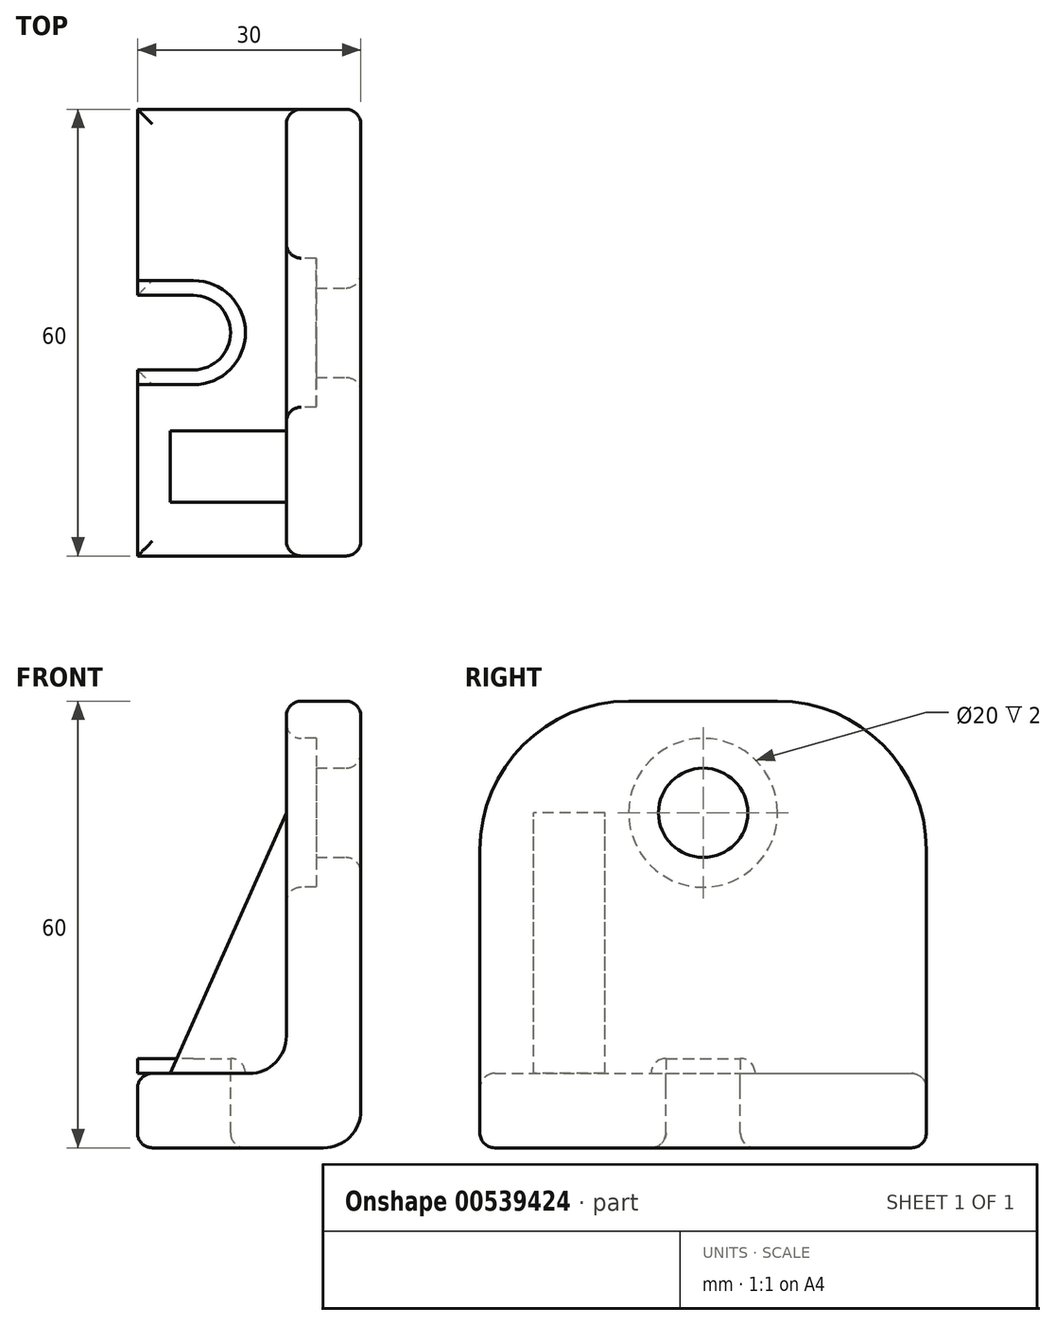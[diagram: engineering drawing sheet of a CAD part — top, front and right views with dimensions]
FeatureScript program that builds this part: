
annotation { "Feature Type Name" : "Feature", "Feature Type Description" : "" }
export const myFeature = defineFeature(function(context is Context, id is Id, definition is map)
    precondition{}
    {
        {
            var Q0;
            Q0=qCreatedBy(makeId("Front.planeOp"),FACE);
            var sketch = newSketch(context, id + "F0", { "sketchPlane" : qUnion([Q0])});
            skLineSegment(sketch, "E0", {"start": v(0, 0) * mm, "end": v(0, 10) * mm});
            skLineSegment(sketch, "E1", {"start": v(0, 10) * mm, "end": v(15, 10) * mm});
            skLineSegment(sketch, "E2", {"start": v(20, 15) * mm, "end": v(20, 60) * mm});
            skLineSegment(sketch, "E3", {"start": v(20, 60) * mm, "end": v(30, 60) * mm});
            skLineSegment(sketch, "E4", {"start": v(30, 60) * mm, "end": v(30, 5) * mm});
            skLineSegment(sketch, "E5", {"start": v(25, 0) * mm, "end": v(0, 0) * mm});
            skPoint(sketch, "E6.visualSharp", {"position": v(20, 10) * mm});
            skArc(sketch, "E6.filletArc", {"start": v(15, 10) * mm, "mid": v(18.54, 11.46) * mm, "end": v(20, 15) * mm});
            skPoint(sketch, "E7.visualSharp", {"position": v(30, 0) * mm});
            skArc(sketch, "E7.filletArc", {"start": v(25, 0) * mm, "mid": v(28.54, 1.46) * mm, "end": v(30, 5) * mm});
            skSolve(sketch);
        }
        {
            var Q0;
            Q0=makeQuery(id+"F0.imprint","IMPRINT",FACE,{"disambiguationData":[TD([[makeQuery(id+"F0.imprint","IMPRINT",EDGE,{"derivedFrom":sQuery(id+"F0.wireOp",EDGE,"E0")}),-1.0]])]});
            extrude(context, id + "F1", {"entities" : qUnion([Q0]), "endBound" : BoundingType.SYMMETRIC, "depth" : 60 * mm, "offsetDistance" : 25 * mm});
        }
        {
            var Q0;
            Q0=makeQuery(id+"F1.opExtrude","SWEPT_FACE",FACE,{"disambiguationData":[OSD([sQuery(id+"F0.wireOp",EDGE,"E4")])]});
            var sketch = newSketch(context, id + "F2", { "sketchPlane" : qUnion([Q0])});
            skCircle(sketch, "E8", {"center": v(0, 45) * mm, "radius": 6 * mm});
            skSolve(sketch);
        }
        {
            var Q0;
            Q0=makeQuery(id+"F2.imprint","IMPRINT",FACE,{"disambiguationData":[TD([[makeQuery(id+"F2.imprint","IMPRINT",EDGE,{"derivedFrom":sQuery(id+"F2.wireOp",EDGE,"E8")}),1.0]])]});
            var Q1;
            Q1=makeQuery(id+"F1.opExtrude","SWEPT_FACE",FACE,{"disambiguationData":[OSD([sQuery(id+"F0.wireOp",EDGE,"E2")])]});
            extrude(context, id + "F3", {"entities" : qUnion([Q0]), "operationType" : NewBodyOperationType.REMOVE, "endBound" : BoundingType.UP_TO_SURFACE, "oppositeDirection" : true, "depth" : 25 * mm, "endBoundEntityFace" : qUnion([Q1]), "offsetDistance" : 25 * mm});
        }
        {
            var Q0;
            Q0=makeQuery(id+"F1.opExtrude","SWEPT_FACE",FACE,{"disambiguationData":[OSD([sQuery(id+"F0.wireOp",EDGE,"E2")])]});
            var sketch = newSketch(context, id + "F4", { "sketchPlane" : qUnion([Q0])});
            skCircle(sketch, "E9", {"center": v(0, 45) * mm, "radius": 10 * mm});
            skSolve(sketch);
        }
        {
            var Q0;
            Q0 = qSketchRegion(id + "F4", true);
            extrude(context, id + "F5", {"entities" : qUnion([Q0]), "operationType" : NewBodyOperationType.REMOVE, "oppositeDirection" : true, "depth" : 4 * mm, "offsetDistance" : 25 * mm});
        }
        {
            var Q0;
            Q0=makeQuery(id+"F1.opExtrude","SWEPT_FACE",FACE,{"disambiguationData":[OSD([sQuery(id+"F0.wireOp",EDGE,"E1")])]});
            var sketch = newSketch(context, id + "F6", { "sketchPlane" : qUnion([Q0])});
            skArc(sketch, "E10", {"start": v(7.5, -5) * mm, "mid": v(12.5, 0) * mm, "end": v(7.5, 5) * mm});
            skLineSegment(sketch, "E11", {"start": v(7.5, 5) * mm, "end": v(0, 5) * mm});
            skLineSegment(sketch, "E12", {"start": v(7.5, -5) * mm, "end": v(0, -5) * mm});
            skLineSegment(sketch, "E13", {"start": v(0, -5) * mm, "end": v(0, 5) * mm});
            skSolve(sketch);
        }
        {
            var Q0;
            Q0=makeQuery(id+"F6.imprint","IMPRINT",FACE,{"disambiguationData":[TD([[makeQuery(id+"F6.imprint","IMPRINT",EDGE,{"derivedFrom":sQuery(id+"F6.wireOp",EDGE,"E10")}),1.0]])]});
            var Q1;
            Q1=makeQuery(id+"F1.opExtrude","SWEPT_FACE",FACE,{"disambiguationData":[OSD([sQuery(id+"F0.wireOp",EDGE,"E5")])]});
            extrude(context, id + "F7", {"entities" : qUnion([Q0]), "operationType" : NewBodyOperationType.REMOVE, "endBound" : BoundingType.UP_TO_SURFACE, "oppositeDirection" : true, "depth" : 25 * mm, "endBoundEntityFace" : qUnion([Q1]), "offsetDistance" : 25 * mm});
        }
        {
            var Q0;
            Q0=qCreatedBy(makeId("Front.planeOp"),FACE);
            cPlane(context, id + "F8", {"entities" : qUnion([Q0]), "cplaneType" : CPlaneType.OFFSET, "offset" : 18 * mm, "width" : 150 * mm, "height" : 150 * mm});
        }
        {
            var Q0;
            Q0=qCreatedBy(id+"F8.planeOp",FACE);
            var sketch = newSketch(context, id + "F9", { "sketchPlane" : qUnion([Q0])});
            skLineSegment(sketch, "E14.0", {"start": v(20, 15) * mm, "end": v(20, 45) * mm});
            skArc(sketch, "E14.1", {"start": v(15, 10) * mm, "mid": v(18.54, 11.46) * mm, "end": v(20, 15) * mm});
            skLineSegment(sketch, "E14.2", {"start": v(4.4, 10) * mm, "end": v(15, 10) * mm});
            skLineSegment(sketch, "E15", {"start": v(4.4, 10) * mm, "end": v(20, 45) * mm});
            skSolve(sketch);
        }
        {
            var Q0;
            Q0 = qSketchRegion(id + "F9", true);
            extrude(context, id + "F10", {"entities" : qUnion([Q0]), "endBound" : BoundingType.SYMMETRIC, "oppositeDirection" : true, "depth" : 9.6 * mm, "offsetDistance" : 25 * mm});
        }
        {
            var Q0;
            Q0=makeQuery(id+"F6.imprint","IMPRINT",FACE,{"disambiguationData":[TD([[makeQuery(id+"F6.imprint","IMPRINT",EDGE,{"derivedFrom":sQuery(id+"F6.wireOp",EDGE,"E10")}),-1.0]])]});
            var sketch = newSketch(context, id + "F11", { "sketchPlane" : qUnion([Q0])});
            skArc(sketch, "E16.0", {"start": v(7.5, -5) * mm, "mid": v(12.5, 0) * mm, "end": v(7.5, 5) * mm});
            skLineSegment(sketch, "E16.1", {"start": v(7.5, -5) * mm, "end": v(0, -5) * mm});
            skLineSegment(sketch, "E16.2", {"start": v(7.5, 5) * mm, "end": v(0, 5) * mm});
            skLineSegment(sketch, "E17.0", {"start": v(7.5, 7) * mm, "end": v(0, 7) * mm});
            skArc(sketch, "E17.1", {"start": v(7.5, -7) * mm, "mid": v(14.5, 0) * mm, "end": v(7.5, 7) * mm});
            skLineSegment(sketch, "E17.2", {"start": v(7.5, -7) * mm, "end": v(0, -7) * mm});
            skLineSegment(sketch, "E18", {"start": v(0, 7) * mm, "end": v(0, 5) * mm});
            skLineSegment(sketch, "E19", {"start": v(0, -5) * mm, "end": v(0, -7) * mm});
            skPoint(sketch, "E16.3.end.orphan", {"position": v(0, 5) * mm});
            skPoint(sketch, "E16.3.start.orphan", {"position": v(0, -5) * mm});
            skSolve(sketch);
        }
        {
            var Q0;
            Q0=makeQuery(id+"F11.imprint","IMPRINT",FACE,{"disambiguationData":[TD([[makeQuery(id+"F11.imprint","IMPRINT",EDGE,{"derivedFrom":sQuery(id+"F11.wireOp",EDGE,"E16.0")}),-1.0]])]});
            extrude(context, id + "F12", {"entities" : qUnion([Q0]), "depth" : 2 * mm, "offsetDistance" : 25 * mm});
        }
        {
            var Q0;
            Q0=makeQuery(id+"F1.opExtrude","CAP_EDGE",EDGE,{"disambiguationData":[OSD([sQuery(id+"F0.wireOp",EDGE,"E3")])],"isStart":true});
            var Q1;
            Q1=makeQuery(id+"F1.opExtrude","CAP_EDGE",EDGE,{"disambiguationData":[OSD([sQuery(id+"F0.wireOp",EDGE,"E3")])],"isStart":false});
            fillet(context, id + "F13", {"entities" : qUnion([Q0, Q1]), "radius" : 20 * mm, "tangentPropagation" : true, "allowEdgeOverflow" : false});
        }
        {
            var Q0;
            Q0=makeQuery(id+"F1.opExtrude","CAP_EDGE",EDGE,{"disambiguationData":[OSD([sQuery(id+"F0.wireOp",EDGE,"E1")])],"isStart":false});
            var Q1;
            {var subQ0=sQuery(id+"F0.wireOp",EDGE,"E0");var subQ1=sQuery(id+"F0.wireOp",EDGE,"E1");Q1=makeQuery(id+"F7.boolean.opBoolean","SPLIT",EDGE,{"disambiguationData":[TD([makeQuery(id+"F7.opExtrude","SWEPT_FACE",FACE,{"disambiguationData":[OSD([sQuery(id+"F6.wireOp",EDGE,"E12")])]})])],"derivedFrom":makeQuery(id+"F1.opExtrude","SWEPT_EDGE",EDGE,{"disambiguationData":[OSD([subQ0,subQ1])]})});}
            var Q2;
            {var subQ0=sQuery(id+"F0.wireOp",EDGE,"E0");var subQ1=sQuery(id+"F0.wireOp",EDGE,"E1");Q2=makeQuery(id+"F7.boolean.opBoolean","SPLIT",EDGE,{"disambiguationData":[TD([makeQuery(id+"F7.opExtrude","SWEPT_FACE",FACE,{"disambiguationData":[OSD([sQuery(id+"F6.wireOp",EDGE,"E11")])]})])],"derivedFrom":makeQuery(id+"F1.opExtrude","SWEPT_EDGE",EDGE,{"disambiguationData":[OSD([subQ0,subQ1])]})});}
            var Q3;
            Q3=makeQuery(id+"F1.opExtrude","SWEPT_FACE",FACE,{"disambiguationData":[OSD([sQuery(id+"F0.wireOp",EDGE,"E2")])]});
            var Q4;
            Q4=makeQuery(id+"F1.opExtrude","SWEPT_FACE",FACE,{"disambiguationData":[OSD([sQuery(id+"F0.wireOp",EDGE,"E4")])]});
            var Q5;
            Q5=makeQuery(id+"F1.opExtrude","SWEPT_FACE",FACE,{"disambiguationData":[OSD([sQuery(id+"F0.wireOp",EDGE,"E5")])]});
            var Q6;
            Q6=makeQuery(id+"F12.opExtrude","CAP_EDGE",EDGE,{"disambiguationData":[OSD([sQuery(id+"F11.wireOp",EDGE,"E17.2")])],"isStart":false});
            var Q7;
            Q7=makeQuery(id+"F12.opExtrude","CAP_EDGE",EDGE,{"disambiguationData":[OSD([sQuery(id+"F11.wireOp",EDGE,"E17.1")])],"isStart":false});
            fillet(context, id + "F14", {"entities" : qUnion([Q0, Q1, Q2, Q3, Q4, Q5, Q6, Q7]), "radius" : 2 * mm, "tangentPropagation" : true, "allowEdgeOverflow" : false});
        }
    });
